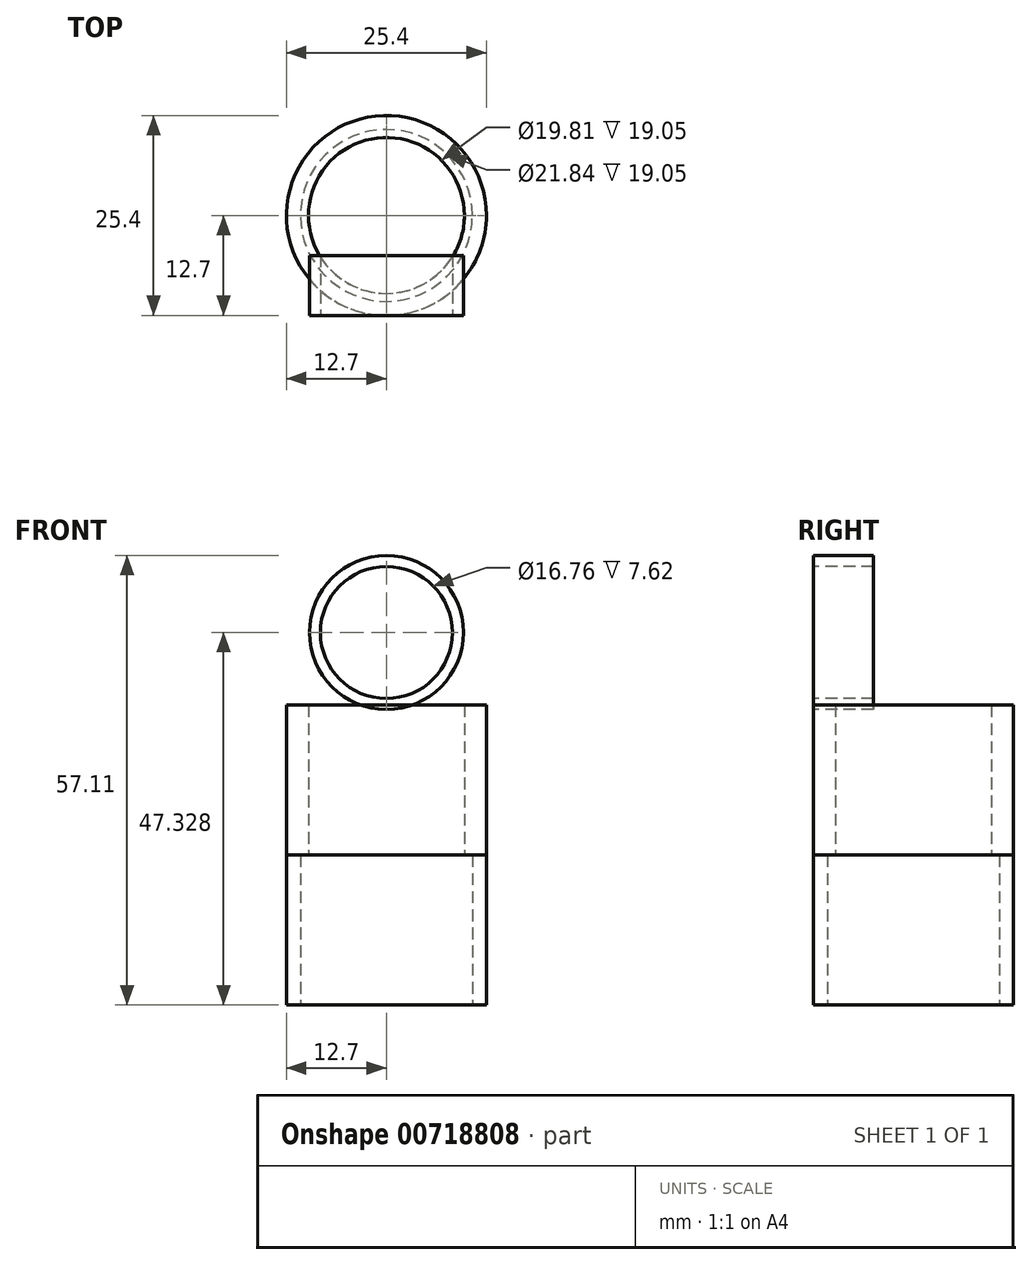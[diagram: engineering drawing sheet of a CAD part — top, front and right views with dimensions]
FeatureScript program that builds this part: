
annotation { "Feature Type Name" : "Feature", "Feature Type Description" : "" }
export const myFeature = defineFeature(function(context is Context, id is Id, definition is map)
    precondition{}
    {
        {
            var Q0;
            Q0=qCreatedBy(makeId("Top.planeOp"),FACE);
            var sketch = newSketch(context, id + "F0", { "sketchPlane" : qUnion([Q0])});
            skCircle(sketch, "E0", {"center": v(-25.4, 25.4) * mm, "radius": 10.92 * mm});
            skCircle(sketch, "E1", {"center": v(-25.4, 25.4) * mm, "radius": 12.7 * mm});
            skSolve(sketch);
        }
        {
            var Q0;
            Q0 = qSketchRegion(id + "F0", true);
            extrude(context, id + "F1", {"entities" : qUnion([Q0]), "depth" : 19.05 * mm, "offsetDistance" : 25.4 * mm});
        }
        {
            var Q0;
            Q0=qCreatedBy(makeId("Front.planeOp"),FACE);
            cPlane(context, id + "F2", {"entities" : qUnion([Q0]), "cplaneType" : CPlaneType.OFFSET, "offset" : 12.7 * mm, "oppositeDirection" : true, "width" : 152.4 * mm, "height" : 152.4 * mm});
        }
        {
            var Q0;
            Q0=qCreatedBy(id+"F2.planeOp",FACE);
            var sketch = newSketch(context, id + "F3", { "sketchPlane" : qUnion([Q0])});
            skLineSegment(sketch, "E2", {"start": v(0, 0) * mm, "end": v(-25.4, 0) * mm});
            skCircle(sketch, "E3", {"center": v(-25.4, 47.33) * mm, "radius": 8.38 * mm});
            skCircle(sketch, "E4", {"center": v(-25.4, 47.33) * mm, "radius": 9.78 * mm});
            skSolve(sketch);
        }
        {
            var Q0;
            Q0 = qSketchRegion(id + "F3", true);
            extrude(context, id + "F4", {"entities" : qUnion([Q0]), "operationType" : NewBodyOperationType.ADD, "oppositeDirection" : true, "depth" : 7.62 * mm, "offsetDistance" : 25.4 * mm});
        }
        {
            var Q0;
            Q0=makeQuery(id+"F1.opExtrude","CAP_FACE",FACE,{"disambiguationData":[OSD([sQuery(id+"F0.wireOp",EDGE,"E0"),sQuery(id+"F0.wireOp",EDGE,"E1")])],"isStart":false});
            var sketch = newSketch(context, id + "F5", { "sketchPlane" : qUnion([Q0])});
            skCircle(sketch, "E5", {"center": v(-25.4, 25.4) * mm, "radius": 12.7 * mm});
            skCircle(sketch, "E6", {"center": v(-25.4, 25.4) * mm, "radius": 9.9 * mm});
            skSolve(sketch);
        }
        {
            var Q0;
            Q0 = qSketchRegion(id + "F5", true);
            extrude(context, id + "F6", {"entities" : qUnion([Q0]), "depth" : 19.05 * mm, "offsetDistance" : 25.4 * mm});
        }
    });
